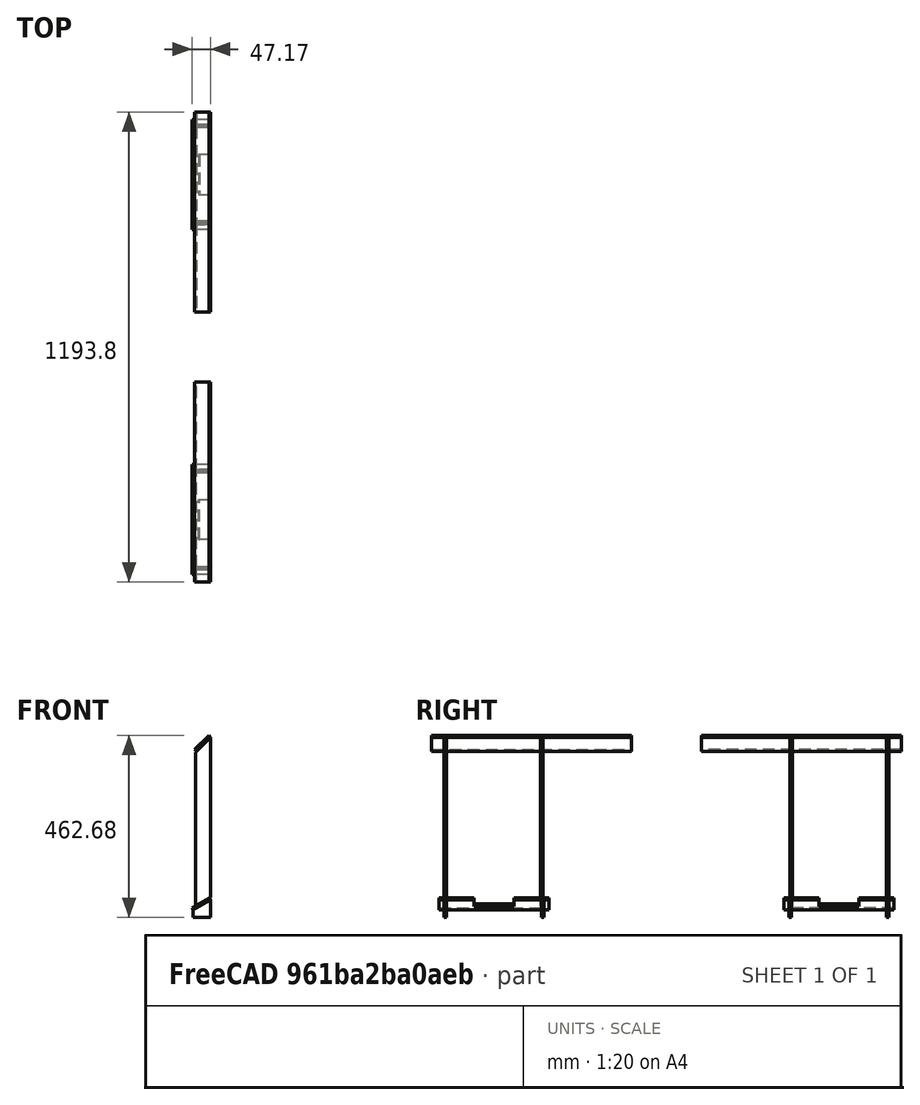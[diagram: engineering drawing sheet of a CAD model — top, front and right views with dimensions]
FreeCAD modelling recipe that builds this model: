
FCSTD DOCUMENT  (FreeCAD 0.17R13522 (Git))
Label: ssqa module
License: CreativeCommons Attribution
LicenseURL: http://creativecommons.org/licenses/by/4.0/
objects: App::FeaturePython×25, Part::FeaturePython×6, Part::MultiFuse×2, Part::Mirroring×1
note: 9 computed .brp shape members not serialized (recipe doc carries the construction recipe); baked Part::Feature solids carry a one-line shape summary decoded from their .brp

FEATURE [Part::FeaturePython] ssqa_bottom_bar_01  # a2plus imported part (geometry in sourceFile) (typed FeaturePython)
  Placement = pos=(-9.06909,0,-419.256) rot=(-0.250563,-0.250563,0.935113;1.63783rad)
  fixedPosition = false
  sourceFile = <userpath>/Freecad_Git/Grapples/01_Hardware/Mechanical_Parts/CAD/ssqa bottom bar.fcstd
  timeLastImport = 1.52682e+09
  updateColors = true
FEATURE [Part::FeaturePython] ssqa_side_bar_01  # a2plus imported part (geometry in sourceFile) (typed FeaturePython)
  Placement = pos=(-9.06909,12.7,-5.52369) rot=(0,0.707107,0.707107;3.14159rad)
  fixedPosition = true
  sourceFile = <userpath>/Freecad_Git/Grapples/01_Hardware/Mechanical_Parts/CAD/ssqa side bar.fcstd
  timeLastImport = 1.52682e+09
  updateColors = true
FEATURE [Part::FeaturePython] ssqa_top_bar_01  # a2plus imported part (geometry in sourceFile) (typed FeaturePython)
  Placement = pos=(-9.06909,-19.05,-5.52369) rot=(-0.357407,-0.357407,0.862856;1.71777rad)
  fixedPosition = false
  sourceFile = <userpath>/Freecad_Git/Grapples/01_Hardware/Mechanical_Parts/CAD/ssqa top bar.fcstd
  timeLastImport = 1.52682e+09
  updateColors = true
FEATURE [Part::FeaturePython] ssqa_bottom_brace_01  # a2plus imported part (geometry in sourceFile) (typed FeaturePython)
  Placement = pos=(-9.06909,12.7,-463.706) rot=(0,0.707107,0.707107;3.14159rad)
  fixedPosition = false
  sourceFile = <userpath>/Freecad_Git/Grapples/01_Hardware/Mechanical_Parts/CAD/ssqa bottom brace.fcstd
  timeLastImport = 1.5306e+09
  updateColors = true
FEATURE [App::FeaturePython] planeConstraint02_mirror001  label="planeConstraint02__ssqa_bottom_bar_01"  # a2plus constraint (typed FeaturePython)
  Object1 = ssqa_bottom_bar_01
  Object2 = ssqa_side_bar_01
  SubElement1 = Face1
  SubElement2 = Face5
  Type = plane
  directionConstraint = 0
  offset = -12.7
FEATURE [App::FeaturePython] planeConstraint04  label="planeConstraint04__ssqa_top_bar_01"  # a2plus constraint (typed FeaturePython)
  Object1 = ssqa_side_bar_01
  Object2 = ssqa_top_bar_01
  SubElement1 = Face4
  SubElement2 = Face5
  Type = plane
  directionConstraint = 1
  offset = 0
FEATURE [App::FeaturePython] planeConstraint04_mirror  label="planeConstraint04__ssqa_side_bar_01"  # a2plus constraint (typed FeaturePython)
  Object1 = ssqa_side_bar_01
  Object2 = ssqa_top_bar_01
  SubElement1 = Face4
  SubElement2 = Face5
  Type = plane
  directionConstraint = 1
  offset = 0
FEATURE [App::FeaturePython] planeConstraint05  label="planeConstraint05__ssqa_top_bar_01"  # a2plus constraint (typed FeaturePython)
  Object1 = ssqa_side_bar_01
  Object2 = ssqa_top_bar_01
  SubElement1 = Face5
  SubElement2 = Face1
  Type = plane
  directionConstraint = 0
  offset = 31.75
FEATURE [App::FeaturePython] planeConstraint05_mirror  label="planeConstraint05__ssqa_side_bar_01"  # a2plus constraint (typed FeaturePython)
  Object1 = ssqa_side_bar_01
  Object2 = ssqa_top_bar_01
  SubElement1 = Face5
  SubElement2 = Face1
  Type = plane
  directionConstraint = 0
  offset = 31.75
FEATURE [Part::FeaturePython] ssqa_bottom_brace_02  # a2plus imported part (geometry in sourceFile) (typed FeaturePython)
  Placement = pos=(-9.06909,260.35,-463.706) rot=(0,0.707107,0.707107;3.14159rad)
  fixedPosition = false
  sourceFile = <userpath>/Freecad_Git/Grapples/01_Hardware/Mechanical_Parts/CAD/ssqa bottom brace.fcstd
  timeLastImport = 1.5306e+09
  updateColors = true
FEATURE [App::FeaturePython] planeConstraint06  label="planeConstraint06__ssqa_top_bar_01"  # a2plus constraint (typed FeaturePython)
  Object1 = ssqa_side_bar_01
  Object2 = ssqa_top_bar_01
  SubElement1 = Face1
  SubElement2 = Vertex2
  Type = plane
  directionConstraint = 0
  offset = 0
FEATURE [App::FeaturePython] planeConstraint06_mirror  label="planeConstraint06__ssqa_side_bar_01"  # a2plus constraint (typed FeaturePython)
  Object1 = ssqa_side_bar_01
  Object2 = ssqa_top_bar_01
  SubElement1 = Face1
  SubElement2 = Vertex2
  Type = plane
  directionConstraint = 0
  offset = 0
FEATURE [App::FeaturePython] planeConstraint01  label="planeConstraint01__ssqa_side_bar_01"  # a2plus constraint (typed FeaturePython)
  Object1 = ssqa_bottom_bar_01
  Object2 = ssqa_side_bar_01
  SubElement1 = Face3
  SubElement2 = Face2
  Type = plane
  directionConstraint = 0
  offset = 0
FEATURE [App::FeaturePython] planeConstraint01_mirror  label="planeConstraint01__ssqa_bottom_bar_01"  # a2plus constraint (typed FeaturePython)
  Object1 = ssqa_bottom_bar_01
  Object2 = ssqa_side_bar_01
  SubElement1 = Face3
  SubElement2 = Face2
  Type = plane
  directionConstraint = 0
  offset = 0
FEATURE [App::FeaturePython] planeConstraint02  label="planeConstraint02__ssqa_bottom_bar_002"  # a2plus constraint (typed FeaturePython)
  Object1 = ssqa_side_bar_01
  Object2 = ssqa_bottom_bar_01
  SubElement1 = Face1
  SubElement2 = Vertex2
  Type = plane
  directionConstraint = 0
  offset = 0
FEATURE [App::FeaturePython] planeConstraint02_mirror  label="planeConstraint02__ssqa_side_bar_01"  # a2plus constraint (typed FeaturePython)
  Object1 = ssqa_side_bar_01
  Object2 = ssqa_bottom_bar_01
  SubElement1 = Face1
  SubElement2 = Vertex2
  Type = plane
  directionConstraint = 0
  offset = 0
FEATURE [App::FeaturePython] planeConstraint03  label="planeConstraint03__ssqa_bottom_bar_01"  # a2plus constraint (typed FeaturePython)
  Object1 = ssqa_side_bar_01
  Object2 = ssqa_bottom_bar_01
  SubElement1 = Face5
  SubElement2 = Face1
  Type = plane
  directionConstraint = 0
  offset = 12.7
FEATURE [App::FeaturePython] planeConstraint03_mirror  label="planeConstraint03__ssqa_side_bar_01"  # a2plus constraint (typed FeaturePython)
  Object1 = ssqa_side_bar_01
  Object2 = ssqa_bottom_bar_01
  SubElement1 = Face5
  SubElement2 = Face1
  Type = plane
  directionConstraint = 0
  offset = 12.7
FEATURE [App::FeaturePython] planeConstraint07  label="planeConstraint07__ssqa_bottom_brace_01"  # a2plus constraint (typed FeaturePython)
  Object1 = ssqa_bottom_bar_01
  Object2 = ssqa_bottom_brace_01
  SubElement1 = Face5
  SubElement2 = Face3
  Type = plane
  directionConstraint = 1
  offset = 0
FEATURE [App::FeaturePython] planeConstraint07_mirror  label="planeConstraint07__ssqa_bottom_bar_01"  # a2plus constraint (typed FeaturePython)
  Object1 = ssqa_bottom_bar_01
  Object2 = ssqa_bottom_brace_01
  SubElement1 = Face5
  SubElement2 = Face3
  Type = plane
  directionConstraint = 1
  offset = 0
FEATURE [App::FeaturePython] planeConstraint08  label="planeConstraint08__ssqa_side_bar_01"  # a2plus constraint (typed FeaturePython)
  Object1 = ssqa_bottom_brace_01
  Object2 = ssqa_side_bar_01
  SubElement1 = Face5
  SubElement2 = Face5
  Type = plane
  directionConstraint = 0
  offset = 0
FEATURE [App::FeaturePython] planeConstraint08_mirror  label="planeConstraint08__ssqa_bottom_brace_01"  # a2plus constraint (typed FeaturePython)
  Object1 = ssqa_bottom_brace_01
  Object2 = ssqa_side_bar_01
  SubElement1 = Face5
  SubElement2 = Face5
  Type = plane
  directionConstraint = 0
  offset = 0
FEATURE [App::FeaturePython] planeConstraint09  label="planeConstraint09__ssqa_side_bar_01"  # a2plus constraint (typed FeaturePython)
  Object1 = ssqa_bottom_brace_01
  Object2 = ssqa_side_bar_01
  SubElement1 = Face4
  SubElement2 = Face1
  Type = plane
  directionConstraint = 0
  offset = 0
FEATURE [App::FeaturePython] planeConstraint09_mirror  label="planeConstraint09__ssqa_bottom_brace_01"  # a2plus constraint (typed FeaturePython)
  Object1 = ssqa_bottom_brace_01
  Object2 = ssqa_side_bar_01
  SubElement1 = Face4
  SubElement2 = Face1
  Type = plane
  directionConstraint = 0
  offset = 0
FEATURE [App::FeaturePython] planeConstraint10  label="planeConstraint10__ssqa_bottom_bar_01"  # a2plus constraint (typed FeaturePython)
  Object1 = ssqa_bottom_brace_02
  Object2 = ssqa_bottom_bar_01
  SubElement1 = Face3
  SubElement2 = Face5
  Type = plane
  directionConstraint = 1
  offset = 0
FEATURE [App::FeaturePython] planeConstraint10_mirror  label="planeConstraint10__ssqa_bottom_brace_02"  # a2plus constraint (typed FeaturePython)
  Object1 = ssqa_bottom_brace_02
  Object2 = ssqa_bottom_bar_01
  SubElement1 = Face3
  SubElement2 = Face5
  Type = plane
  directionConstraint = 1
  offset = 0
FEATURE [App::FeaturePython] planeConstraint11  label="planeConstraint11__ssqa_bottom_brace_01"  # a2plus constraint (typed FeaturePython)
  Object1 = ssqa_bottom_brace_02
  Object2 = ssqa_bottom_brace_01
  SubElement1 = Face4
  SubElement2 = Face4
  Type = plane
  directionConstraint = 0
  offset = 0
FEATURE [App::FeaturePython] planeConstraint11_mirror  label="planeConstraint11__ssqa_bottom_brace_02"  # a2plus constraint (typed FeaturePython)
  Object1 = ssqa_bottom_brace_02
  Object2 = ssqa_bottom_brace_01
  SubElement1 = Face4
  SubElement2 = Face4
  Type = plane
  directionConstraint = 0
  offset = 0
FEATURE [App::FeaturePython] planeConstraint12  label="planeConstraint12__ssqa_bottom_bar_01"  # a2plus constraint (typed FeaturePython)
  Object1 = ssqa_bottom_brace_02
  Object2 = ssqa_bottom_bar_01
  SubElement1 = Face6
  SubElement2 = Face7
  Type = plane
  directionConstraint = 0
  offset = -12.7
FEATURE [App::FeaturePython] planeConstraint12_mirror  label="planeConstraint12__ssqa_bottom_brace_02"  # a2plus constraint (typed FeaturePython)
  Object1 = ssqa_bottom_brace_02
  Object2 = ssqa_bottom_bar_01
  SubElement1 = Face6
  SubElement2 = Face7
  Type = plane
  directionConstraint = 0
  offset = -12.7
FEATURE [Part::FeaturePython] Clone  label="ssqa_side_bar_002"  # Draft clone (typed FeaturePython)
  AttacherType = Attacher::AttachEngine3D
  Fuse = false
  Objects = -> [ssqa_side_bar_01]
  Placement = pos=(-9.06909,258.369,-5.52369) rot=(0,0.707107,0.707107;3.14159rad)
  Scale = (1,1,1)
FEATURE [Part::MultiFuse] Fusion
  Placement = pos=(0,-577.85,0) rot=(0,0,1;0rad)
  Shapes = -> [ssqa_bottom_bar_01,ssqa_side_bar_01,ssqa_top_bar_01,ssqa_bottom_brace_01,ssqa_bottom_brace_02,Clone]
FEATURE [Part::Mirroring] Part__Mirroring  label="Fusion (Mirror #1)"
  Base = (0,0,0)
  Normal = (0,1,0)
  Source = -> Fusion
FEATURE [Part::MultiFuse] Fusion001
  Shapes = -> [Part__Mirroring,Fusion]
